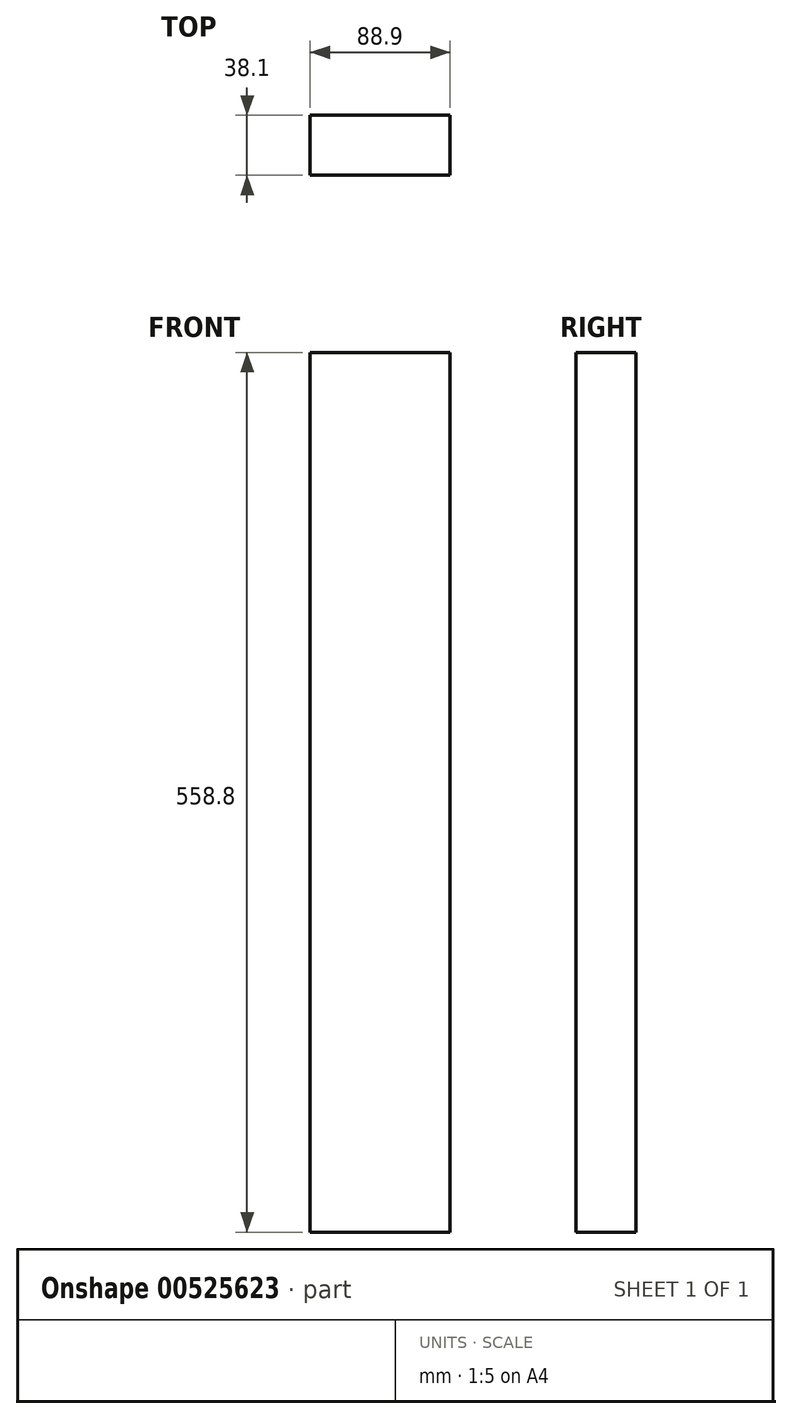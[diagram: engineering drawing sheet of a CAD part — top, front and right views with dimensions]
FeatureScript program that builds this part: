
annotation { "Feature Type Name" : "Feature", "Feature Type Description" : "" }
export const myFeature = defineFeature(function(context is Context, id is Id, definition is map)
    precondition{}
    {
        {
            var Q0;
            Q0=qCreatedBy(makeId("Top.planeOp"),FACE);
            var sketch = newSketch(context, id + "F0", { "sketchPlane" : qUnion([Q0])});
            skLineSegment(sketch, "E0.bottom", {"start": v(44.45, -19.05) * mm, "end": v(-44.45, -19.05) * mm});
            skLineSegment(sketch, "E0.top", {"start": v(44.45, 19.05) * mm, "end": v(-44.45, 19.05) * mm});
            skLineSegment(sketch, "E0.left", {"start": v(44.45, -19.05) * mm, "end": v(44.45, 19.05) * mm});
            skLineSegment(sketch, "E0.right", {"start": v(-44.45, -19.05) * mm, "end": v(-44.45, 19.05) * mm});
            skPoint(sketch, "E0.middle", {"position": v(0, 0) * mm});
            skSolve(sketch);
        }
        {
            var Q0;
            Q0 = qSketchRegion(id + "F0", true);
            extrude(context, id + "F1", {"entities" : qUnion([Q0]), "depth" : 558.8 * mm, "offsetDistance" : 25.4 * mm});
        }
    });
